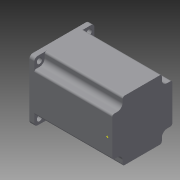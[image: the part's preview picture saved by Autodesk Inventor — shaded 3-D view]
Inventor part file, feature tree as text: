
AUTODESK INVENTOR PART (.ipt)
format: ipt  version: 2013 (Build 170138000, 138)  size: 190,464 bytes
history: native  units: in
note: dims shown in document units (in); Inventor stores cm internally (conversion verified against a paired STEP export)
features: extrude x5, sketch x5, other x1, fillet x1, hole x1, projected_geometry x1
ambient origin geometry x8: Origin, YZ Plane, XZ Plane, XY Plane, X Axis, Y Axis, Z Axis, Center Point
bodies: Solid1 (feature_tree)
feature tree (14):
  extrude  "Extrusion1"  Depth=2.25in
  extrude  "Extrusion2"  Depth=1.5in
  extrude  "Extrusion3"  Depth=0.25in
  extrude  "Extrusion4"  Depth=0.23in
  other  "motorLead"
  extrude  "Extrusion6"  Depth=0.125in
  fillet  "Fillet1"  Radius=1.125in
  hole  "Hole1"  [1 undecoded]
  sketch  "Sketch1"  dims[d0=2.25in d1=2.25in]
  sketch  "Sketch2"  dims[d2=3.1in d3=0.0in d4=1.5in]
  sketch  "Sketch3"  dims[d8=0.06in d9=0.0in d10=0.25in]
  sketch  "Sketch4"  dims[d11=0.75in d12=0.0in d13=0.23in]
  sketch  "Sketch6"  dims[d15=0.59in d16=0.0in d17=0.125in d18=1.125in d19=1.125in d33=2.915in d34=0.0in d35=0.075in d36=1.86in d37=1.86in d39=0.195in d40=0.195in d41=0.2in d42=0.75in d43=0.375in d44=0.25in d45=0.5635in d46=1.0in d47=0.8108in d48=0.195in d49=0.195in d50=0.2in d51=0.39in d52=0.39in d53=0.39in d54=0.39in d55=0.39in d56=0.39in d57=0.39in d58=0.39in d59=0.39in d60=0.39in d61=0.39in d62=0.39in d63=0.39in]
  projected_geometry  "Projected Loop1"
note: 1 required parameter value undecoded (feature->parameter linkage not recoverable at this tier; creation-order binding heuristic only, values carry confidence <= 0.55)
